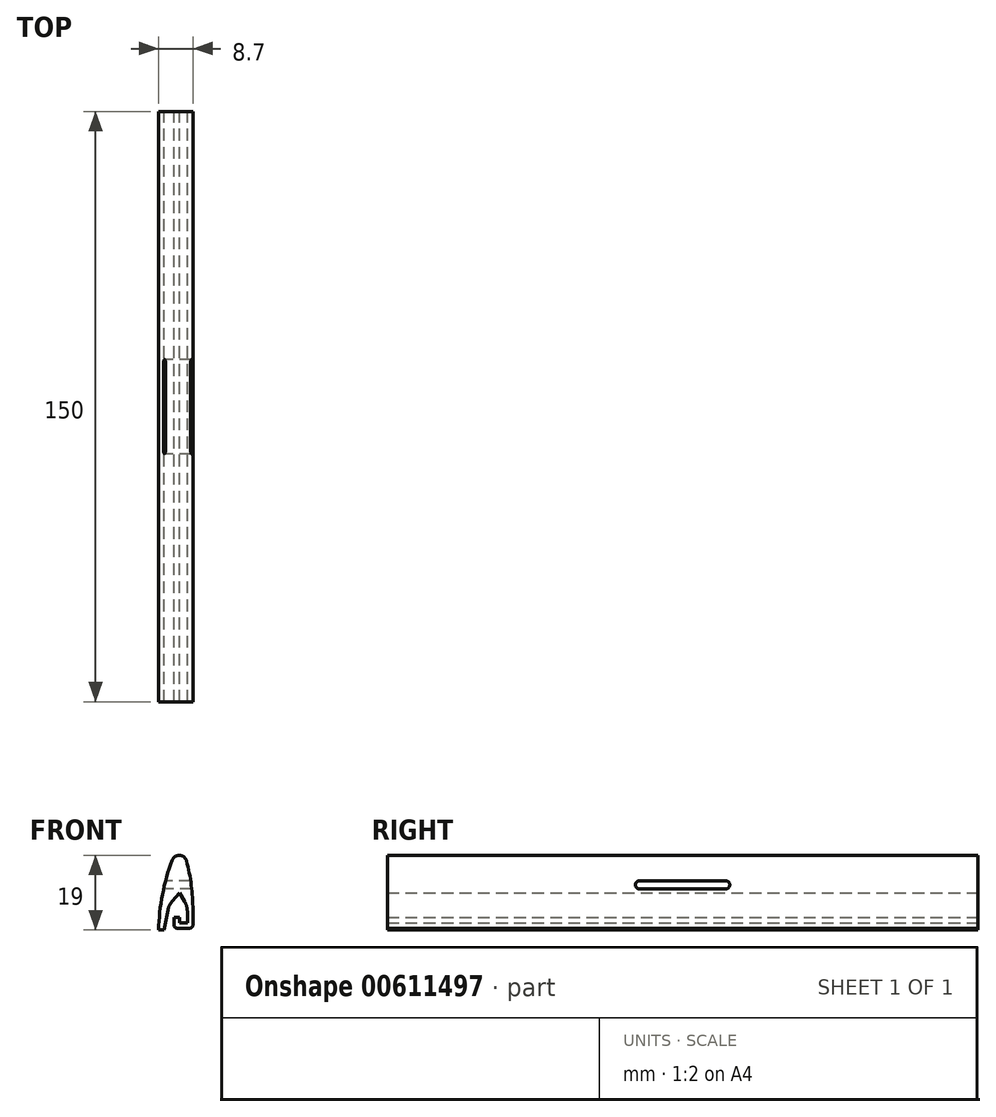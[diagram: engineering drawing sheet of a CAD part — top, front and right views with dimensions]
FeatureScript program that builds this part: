
annotation { "Feature Type Name" : "Feature", "Feature Type Description" : "" }
export const myFeature = defineFeature(function(context is Context, id is Id, definition is map)
    precondition{}
    {
        {
            var Q0;
            Q0=qCreatedBy(makeId("Front.planeOp"),FACE);
            var sketch = newSketch(context, id + "F0", { "sketchPlane" : qUnion([Q0])});
            skLineSegment(sketch, "E0", {"start": v(-1.4, 9) * mm, "end": v(1.4, 9) * mm});
            skPoint(sketch, "E1.orphan", {"position": v(1.4, 0) * mm});
            skLineSegment(sketch, "E2", {"start": v(3.4, -4.87) * mm, "end": v(3.4, -8.75) * mm});
            skLineSegment(sketch, "E3", {"start": v(2.65, -9.5) * mm, "end": v(-0.65, -9.5) * mm});
            skLineSegment(sketch, "E4", {"start": v(-1.4, -8.75) * mm, "end": v(-1.4, -6.7) * mm});
            skLineSegment(sketch, "E5.0", {"start": v(0, -0.52) * mm, "end": v(1.3, -2.7) * mm});
            skLineSegment(sketch, "E6.0", {"start": v(2, -5.26) * mm, "end": v(2, -8.1) * mm});
            skLineSegment(sketch, "E7.0", {"start": v(2, -8.1) * mm, "end": v(0, -8.1) * mm});
            skLineSegment(sketch, "E8.0", {"start": v(0, -8.1) * mm, "end": v(0, -6.7) * mm});
            skLineSegment(sketch, "E9", {"start": v(-1.4, -6.7) * mm, "end": v(0, -6.7) * mm});
            skPoint(sketch, "E10.visualSharp", {"position": v(-4, -3) * mm});
            skLineSegment(sketch, "E11.0", {"start": v(-2.9, -4.73) * mm, "end": v(-3.88, -10) * mm});
            skArc(sketch, "E12.0", {"start": v(-1.87, -2.69) * mm, "mid": v(-2.54, -3.7) * mm, "end": v(-2.92, -4.86) * mm});
            skLineSegment(sketch, "E13.0", {"start": v(0, -0.52) * mm, "end": v(-1.87, -2.69) * mm});
            skLineSegment(sketch, "E14", {"start": v(-5.3, -10) * mm, "end": v(-3.88, -10) * mm});
            skPoint(sketch, "E15.visualSharp", {"position": v(3.4, -3.5) * mm});
            skPoint(sketch, "E16.visualSharp", {"position": v(2, -3.88) * mm});
            skArc(sketch, "E16.filletArc", {"start": v(2, -5.26) * mm, "mid": v(1.82, -3.93) * mm, "end": v(1.3, -2.7) * mm});
            skPoint(sketch, "E17.visualSharp", {"position": v(3.4, -9.5) * mm});
            skArc(sketch, "E17.filletArc", {"start": v(2.65, -9.5) * mm, "mid": v(3.18, -9.28) * mm, "end": v(3.4, -8.75) * mm});
            skPoint(sketch, "E18.visualSharp", {"position": v(-1.4, -9.5) * mm});
            skArc(sketch, "E18.filletArc", {"start": v(-1.4, -8.75) * mm, "mid": v(-1.18, -9.28) * mm, "end": v(-0.65, -9.5) * mm});
            skArc(sketch, "E19", {"start": v(-1.4, 9) * mm, "mid": v(-4.2, -0.33) * mm, "end": v(-5.3, -10) * mm});
            skArc(sketch, "E20", {"start": v(3.4, -4.87) * mm, "mid": v(2.9, 2.13) * mm, "end": v(1.4, 9) * mm});
            skSolve(sketch);
        }
        {
            var Q0;
            Q0=qSketchRegion(id+"F0",true);
            extrude(context, id + "F1", {"entities" : qUnion([Q0]), "endBound" : BoundingType.SYMMETRIC, "depth" : 150 * mm, "offsetDistance" : 25 * mm});
        }
        {
            var Q0;
            Q0=qCreatedBy(makeId("Right.planeOp"),FACE);
            var sketch = newSketch(context, id + "F2", { "sketchPlane" : qUnion([Q0])});
            skLineSegment(sketch, "E21.bottom", {"start": v(11, 2.5) * mm, "end": v(-11, 2.5) * mm});
            skLineSegment(sketch, "E21.top", {"start": v(11, 0.5) * mm, "end": v(-11, 0.5) * mm});
            skLineSegment(sketch, "E21.left", {"start": v(12, 1.5) * mm, "end": v(12, 1.5) * mm});
            skLineSegment(sketch, "E21.right", {"start": v(-12, 1.5) * mm, "end": v(-12, 1.5) * mm});
            skPoint(sketch, "E22.visualSharp", {"position": v(12, 0.5) * mm});
            skArc(sketch, "E22.filletArc", {"start": v(11, 0.5) * mm, "mid": v(11.7, 0.8) * mm, "end": v(12, 1.5) * mm});
            skPoint(sketch, "E23.visualSharp", {"position": v(12, 2.5) * mm});
            skArc(sketch, "E23.filletArc", {"start": v(12, 1.5) * mm, "mid": v(11.7, 2.2) * mm, "end": v(11, 2.5) * mm});
            skPoint(sketch, "E24.visualSharp", {"position": v(-12, 2.5) * mm});
            skArc(sketch, "E24.filletArc", {"start": v(-11, 2.5) * mm, "mid": v(-11.7, 2.2) * mm, "end": v(-12, 1.5) * mm});
            skPoint(sketch, "E25.visualSharp", {"position": v(-12, 0.5) * mm});
            skArc(sketch, "E25.filletArc", {"start": v(-12, 1.5) * mm, "mid": v(-11.7, 0.8) * mm, "end": v(-11, 0.5) * mm});
            skSolve(sketch);
        }
        {
            var Q0;
            Q0=qSketchRegion(id+"F2",true);
            extrude(context, id + "F3", {"entities" : qUnion([Q0]), "operationType" : NewBodyOperationType.REMOVE, "endBound" : BoundingType.SYMMETRIC, "depth" : 25 * mm, "offsetDistance" : 25 * mm});
        }
        {
            var Q0;
            Q0=makeQuery(id+"F1.opExtrude","SWEPT_EDGE",EDGE,{"disambiguationData":[OSD([sQuery(id+"F0.wireOp",EDGE,"E0"),sQuery(id+"F0.wireOp",EDGE,"E19")])]});
            var Q1;
            Q1=makeQuery(id+"F1.opExtrude","SWEPT_EDGE",EDGE,{"disambiguationData":[OSD([sQuery(id+"F0.wireOp",EDGE,"E0"),sQuery(id+"F0.wireOp",EDGE,"E20")])]});
            fillet(context, id + "F4", {"entities" : qUnion([Q0, Q1]), "radius" : 1.9 * mm, "tangentPropagation" : true, "allowEdgeOverflow" : false});
        }
    });
